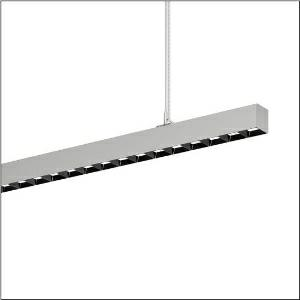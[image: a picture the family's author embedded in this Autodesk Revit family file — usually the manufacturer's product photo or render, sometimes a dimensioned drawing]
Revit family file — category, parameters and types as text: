
# Revit family: silica_r__21_51mx32dc4dsb_d767
name_source: partatom
category: Lighting Fixtures
units: mm (PartAtom-declared; Revit-internal decimal feet)

## family parameters
Cut with Voids When Loaded = No
Host = Face
Light Source = No
Part Type = Normal
Room Calculation Point = No
Round Connector Dimension = Use Diameter
Shared = No

## types (1)
- --- (1 x LED, 18230 lm, 105.8 W, 4000K)
    Apparent Load = 106 VA
    CIE Flux Codes = 86 99 100 59 100
    Color Rendering = 80
    Color Temperature = 4000K
    Default Elevation = 1800 mm
    Description = Silica® 21, office luminaire, primary light control with darklight reflector, of PMMA, black, CAT 2 (L<= 3000cd/m²), light emission: direct/indirect distribution, primary light characteristic: symmetric, installation type: suspended mounting, LED, rated luminous flux: 18.230lm, luminous efficacy: 172lm/W, light colour: 840, colour temperature: 4000K, with terminal, 3+2-pole, max. 2.5mm², mains connection: 220..240V, AC, 50/60Hz, rated input power: 105.8W, luminaire housing, of aluminium, metallic grey (RAL 9006), length: 3.004mm, width: 53mm, height: 53mm, protection rating (complete): IP20, insulation class (complete): insulation class I (protective earthing), certification: CE, permissible operating ambient temperature: 0..+35°C, standard: EN 50419, packaging unit: 1 piece
    Height = 53 mm
    Lamp = 1 x LED
    Lamp Light Flux = 18230 lm
    Lamp Power = 105.8 W
    Lamp count = 1
    Length = 3004 mm
    Luminous efficacy = 172 lm/W
    Manufacturer = Siteco
    ModVariant = No
    Model = 51MX32DC4DSB
    Mounting Place = Ceiling
    Mounting Type = Pendant
    Number of Poles = 1
    OnlyDefault = Yes
    Power Factor = 1
    Product Name = Silica® 21
    Product group = office luminaire | ceiling pendant
    ProductGroupID = 905
    Protection Class = Protection class I
    Protection Degree = IP 20
    RLX_Detail_Level = 1
    RlxData = <blob elided: 65333 chars, md5=45254443>
    Socket = socket
    Standby Power = 0 W
    System Light Flux = 18230 lm
    System Power = 106 W
    Type Comments = factory setting: luminous flux: 100 % | dim-lin: 254 | 366 mA
    Type Image = l_1251731.jpg
    URL = http://relux.com
    VarID = @adj_031169
    Voltage = 0 V
    Weight = 0.00 kg
    Width = 53 mm

## geometry (parser evidence)
native form markers: Blend x4, Sweep x11
no freeform markers — native parametric forms only
